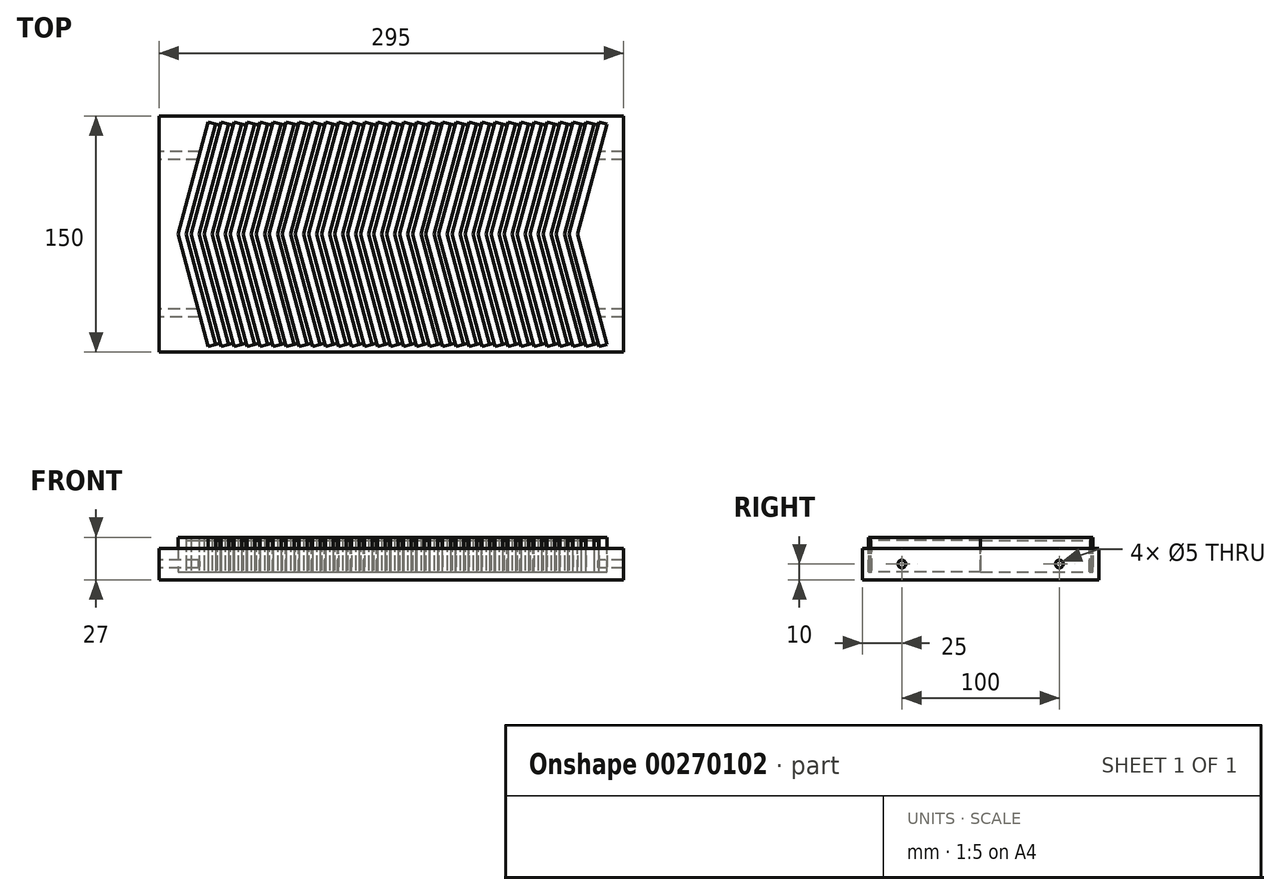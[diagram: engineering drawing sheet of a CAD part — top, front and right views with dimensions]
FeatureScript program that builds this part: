
annotation { "Feature Type Name" : "Feature", "Feature Type Description" : "" }
export const myFeature = defineFeature(function(context is Context, id is Id, definition is map)
    precondition{}
    {
        {
            var Q0;
            Q0=qCreatedBy(makeId("Top.planeOp"),FACE);
            var sketch = newSketch(context, id + "F0", { "sketchPlane" : qUnion([Q0])});
            skLineSegment(sketch, "E0.bottom", {"start": v(147.5, -75) * mm, "end": v(-147.5, -75) * mm});
            skLineSegment(sketch, "E0.top", {"start": v(147.5, 75) * mm, "end": v(-147.5, 75) * mm});
            skLineSegment(sketch, "E0.left", {"start": v(147.5, -75) * mm, "end": v(147.5, 75) * mm});
            skLineSegment(sketch, "E0.right", {"start": v(-147.5, -75) * mm, "end": v(-147.5, 75) * mm});
            skPoint(sketch, "E0.middle", {"position": v(0, 0) * mm});
            skPoint(sketch, "E1", {"position": v(0, 75) * mm});
            skPoint(sketch, "E2", {"position": v(-147.5, 0) * mm});
            skSolve(sketch);
        }
        {
            var Q0;
            Q0=makeQuery(id+"F0.imprint","IMPRINT",FACE,{"disambiguationData":[TD([[makeQuery(id+"F0.imprint","IMPRINT",EDGE,{"derivedFrom":sQuery(id+"F0.wireOp",EDGE,"E0.bottom")}),-1.0]])]});
            extrude(context, id + "F1", {"entities" : qUnion([Q0]), "depth" : 20 * mm});
        }
        {
            var Q0;
            Q0=makeQuery(id+"F1.opExtrude","SWEPT_FACE",FACE,{"disambiguationData":[OSD([sQuery(id+"F0.wireOp",EDGE,"E0.left")])]});
            var sketch = newSketch(context, id + "F2", { "sketchPlane" : qUnion([Q0])});
            skPoint(sketch, "E3", {"position": v(-50, 10) * mm});
            skPoint(sketch, "E4", {"position": v(50, 10) * mm});
            skSolve(sketch);
        }
        {
            var Q0;
            Q0=sQuery(id+"F2.wireOp",VERTEX,"E3");
            var Q1;
            Q1=sQuery(id+"F2.wireOp",VERTEX,"E4");
            var Q2;
            Q2=makeQuery(id+"F1.opExtrude","SWEPT_BODY",BODY,{"disambiguationData":[OSD([sQuery(id+"F0.wireOp",EDGE,"E0.bottom"),sQuery(id+"F0.wireOp",EDGE,"E0.top"),sQuery(id+"F0.wireOp",EDGE,"E0.left"),sQuery(id+"F0.wireOp",EDGE,"E0.right")])]});
            hole(context, id + "F3", {"style" : HoleStyle.SIMPLE, "endStyle" : HoleEndStyle.THROUGH, "standardTappedOrClearance" : lookupTablePath({ "standard" : "ISO", "engagement" : "75%", "pitch" : "1 mm", "size" : "M6", "type" : "Tapped" }), "standardBlindInLast" : lookupTablePath({ "standard" : "ISO", "engagement" : "75%", "pitch" : "1 mm", "size" : "M6", "type" : "Tapped" }), "holeDiameter" : 5 * mm, "showTappedDepth" : true, "tappedDepth" : 40 * mm, "tapClearance" : 3, "startFromSketch" : true, "locations" : qUnion([Q0, Q1]), "scope" : qUnion([Q2]), "majorDiameter" : 6 * mm});
        }
        {
            var Q0;
            Q0=makeQuery(id+"F1.opExtrude","SWEPT_FACE",FACE,{"disambiguationData":[OSD([sQuery(id+"F0.wireOp",EDGE,"E0.right")])]});
            var sketch = newSketch(context, id + "F4", { "sketchPlane" : qUnion([Q0])});
            skPoint(sketch, "E5", {"position": v(0, 10) * mm});
            skLineSegment(sketch, "E6", {"start": v(-50, 10) * mm, "end": v(50, 10) * mm, "construction": true});
            skSolve(sketch);
        }
        {
            var Q0;
            Q0=makeQuery(id+"F1.opExtrude","CAP_FACE",FACE,{"disambiguationData":[OSD([sQuery(id+"F0.wireOp",EDGE,"E0.bottom"),sQuery(id+"F0.wireOp",EDGE,"E0.top"),sQuery(id+"F0.wireOp",EDGE,"E0.left"),sQuery(id+"F0.wireOp",EDGE,"E0.right")])],"isStart":false});
            var sketch = newSketch(context, id + "F5", { "sketchPlane" : qUnion([Q0])});
            skLineSegment(sketch, "E7", {"start": v(-135.5, 0) * mm, "end": v(-116.4, 71.3) * mm});
            skLineSegment(sketch, "E8", {"start": v(-135.5, 0) * mm, "end": v(-116.4, -71.3) * mm});
            skLineSegment(sketch, "E9.0", {"start": v(-130.32, 0) * mm, "end": v(-111.57, 70) * mm});
            skLineSegment(sketch, "E9.1", {"start": v(-130.32, 0) * mm, "end": v(-111.57, -70) * mm});
            skLineSegment(sketch, "E10", {"start": v(-116.4, 71.3) * mm, "end": v(-111.57, 70) * mm});
            skLineSegment(sketch, "E11", {"start": v(-116.4, -71.3) * mm, "end": v(-111.57, -70) * mm});
            skLineSegment(sketch, "E12.0", {"start": v(-127.22, 0) * mm, "end": v(-108.67, 69.22) * mm});
            skLineSegment(sketch, "E12.1", {"start": v(-127.22, 0) * mm, "end": v(-108.67, -69.22) * mm});
            skLineSegment(sketch, "E13", {"start": v(-111.57, 70) * mm, "end": v(-108.67, 69.22) * mm});
            skLineSegment(sketch, "E14", {"start": v(-111.57, -70) * mm, "end": v(-108.67, -69.22) * mm});
            skLineSegment(sketch, "E15.1.0.0", {"start": v(-118.94, 0) * mm, "end": v(-100.39, 69.22) * mm});
            skLineSegment(sketch, "E15.1.0.1", {"start": v(-122.04, 0) * mm, "end": v(-103.28, 70) * mm});
            skLineSegment(sketch, "E15.1.0.2", {"start": v(-127.22, 0) * mm, "end": v(-108.11, 71.3) * mm});
            skLineSegment(sketch, "E15.1.0.3", {"start": v(-127.22, 0) * mm, "end": v(-108.11, -71.3) * mm});
            skLineSegment(sketch, "E15.1.0.4", {"start": v(-122.04, 0) * mm, "end": v(-103.28, -70) * mm});
            skLineSegment(sketch, "E15.1.0.5", {"start": v(-118.94, 0) * mm, "end": v(-100.39, -69.22) * mm});
            skLineSegment(sketch, "E15.1.0.6", {"start": v(-108.11, -71.3) * mm, "end": v(-103.28, -70) * mm});
            skLineSegment(sketch, "E15.1.0.7", {"start": v(-103.28, -70) * mm, "end": v(-100.39, -69.22) * mm});
            skLineSegment(sketch, "E15.1.0.8", {"start": v(-108.11, 71.3) * mm, "end": v(-103.28, 70) * mm});
            skLineSegment(sketch, "E15.1.0.9", {"start": v(-103.28, 70) * mm, "end": v(-100.39, 69.22) * mm});
            skLineSegment(sketch, "E15.2.0.0", {"start": v(-110.65, 0) * mm, "end": v(-92.1, 69.22) * mm});
            skLineSegment(sketch, "E15.2.0.1", {"start": v(-113.76, 0) * mm, "end": v(-95, 70) * mm});
            skLineSegment(sketch, "E15.2.0.2", {"start": v(-118.94, 0) * mm, "end": v(-99.83, 71.3) * mm});
            skLineSegment(sketch, "E15.2.0.3", {"start": v(-118.94, 0) * mm, "end": v(-99.83, -71.3) * mm});
            skLineSegment(sketch, "E15.2.0.4", {"start": v(-113.76, 0) * mm, "end": v(-95, -70) * mm});
            skLineSegment(sketch, "E15.2.0.5", {"start": v(-110.65, 0) * mm, "end": v(-92.1, -69.22) * mm});
            skLineSegment(sketch, "E15.2.0.6", {"start": v(-99.83, -71.3) * mm, "end": v(-95, -70) * mm});
            skLineSegment(sketch, "E15.2.0.7", {"start": v(-95, -70) * mm, "end": v(-92.1, -69.22) * mm});
            skLineSegment(sketch, "E15.2.0.8", {"start": v(-99.83, 71.3) * mm, "end": v(-95, 70) * mm});
            skLineSegment(sketch, "E15.2.0.9", {"start": v(-95, 70) * mm, "end": v(-92.1, 69.22) * mm});
            skLineSegment(sketch, "E15.direction1", {"start": v(-127.22, 0) * mm, "end": v(-118.94, 0) * mm, "construction": true});
            skLineSegment(sketch, "E16.0.3.0", {"start": v(-102.37, 0) * mm, "end": v(-83.82, 69.22) * mm});
            skLineSegment(sketch, "E16.3.3.0", {"start": v(-105.48, 0) * mm, "end": v(-86.72, 70) * mm});
            skLineSegment(sketch, "E16.6.3.0", {"start": v(-110.65, 0) * mm, "end": v(-91.55, 71.3) * mm});
            skLineSegment(sketch, "E16.9.3.0", {"start": v(-110.65, 0) * mm, "end": v(-91.55, -71.3) * mm});
            skLineSegment(sketch, "E16.12.3.0", {"start": v(-105.48, 0) * mm, "end": v(-86.72, -70) * mm});
            skLineSegment(sketch, "E16.15.3.0", {"start": v(-102.37, 0) * mm, "end": v(-83.82, -69.22) * mm});
            skLineSegment(sketch, "E16.18.3.0", {"start": v(-91.55, -71.3) * mm, "end": v(-86.72, -70) * mm});
            skLineSegment(sketch, "E16.21.3.0", {"start": v(-86.72, -70) * mm, "end": v(-83.82, -69.22) * mm});
            skLineSegment(sketch, "E16.24.3.0", {"start": v(-91.55, 71.3) * mm, "end": v(-86.72, 70) * mm});
            skLineSegment(sketch, "E16.27.3.0", {"start": v(-86.72, 70) * mm, "end": v(-83.82, 69.22) * mm});
            skLineSegment(sketch, "E16.0.4.0", {"start": v(-94.09, 0) * mm, "end": v(-75.54, 69.22) * mm});
            skLineSegment(sketch, "E16.3.4.0", {"start": v(-97.2, 0) * mm, "end": v(-78.44, 70) * mm});
            skLineSegment(sketch, "E16.6.4.0", {"start": v(-102.37, 0) * mm, "end": v(-83.27, 71.3) * mm});
            skLineSegment(sketch, "E16.9.4.0", {"start": v(-102.37, 0) * mm, "end": v(-83.27, -71.3) * mm});
            skLineSegment(sketch, "E16.12.4.0", {"start": v(-97.2, 0) * mm, "end": v(-78.44, -70) * mm});
            skLineSegment(sketch, "E16.15.4.0", {"start": v(-94.09, 0) * mm, "end": v(-75.54, -69.22) * mm});
            skLineSegment(sketch, "E16.18.4.0", {"start": v(-83.27, -71.3) * mm, "end": v(-78.44, -70) * mm});
            skLineSegment(sketch, "E16.21.4.0", {"start": v(-78.44, -70) * mm, "end": v(-75.54, -69.22) * mm});
            skLineSegment(sketch, "E16.24.4.0", {"start": v(-83.27, 71.3) * mm, "end": v(-78.44, 70) * mm});
            skLineSegment(sketch, "E16.27.4.0", {"start": v(-78.44, 70) * mm, "end": v(-75.54, 69.22) * mm});
            skLineSegment(sketch, "E16.0.5.0", {"start": v(-85.8, 0) * mm, "end": v(-67.26, 69.22) * mm});
            skLineSegment(sketch, "E16.3.5.0", {"start": v(-88.91, 0) * mm, "end": v(-70.16, 70) * mm});
            skLineSegment(sketch, "E16.6.5.0", {"start": v(-94.09, 0) * mm, "end": v(-74.99, 71.3) * mm});
            skLineSegment(sketch, "E16.9.5.0", {"start": v(-94.09, 0) * mm, "end": v(-74.99, -71.3) * mm});
            skLineSegment(sketch, "E16.12.5.0", {"start": v(-88.91, 0) * mm, "end": v(-70.16, -70) * mm});
            skLineSegment(sketch, "E16.15.5.0", {"start": v(-85.8, 0) * mm, "end": v(-67.26, -69.22) * mm});
            skLineSegment(sketch, "E16.18.5.0", {"start": v(-74.99, -71.3) * mm, "end": v(-70.16, -70) * mm});
            skLineSegment(sketch, "E16.21.5.0", {"start": v(-70.16, -70) * mm, "end": v(-67.26, -69.22) * mm});
            skLineSegment(sketch, "E16.24.5.0", {"start": v(-74.99, 71.3) * mm, "end": v(-70.16, 70) * mm});
            skLineSegment(sketch, "E16.27.5.0", {"start": v(-70.16, 70) * mm, "end": v(-67.26, 69.22) * mm});
            skLineSegment(sketch, "E16.0.6.0", {"start": v(-77.52, 0) * mm, "end": v(-58.98, 69.22) * mm});
            skLineSegment(sketch, "E16.3.6.0", {"start": v(-80.63, 0) * mm, "end": v(-61.87, 70) * mm});
            skLineSegment(sketch, "E16.6.6.0", {"start": v(-85.8, 0) * mm, "end": v(-66.7, 71.3) * mm});
            skLineSegment(sketch, "E16.9.6.0", {"start": v(-85.8, 0) * mm, "end": v(-66.7, -71.3) * mm});
            skLineSegment(sketch, "E16.12.6.0", {"start": v(-80.63, 0) * mm, "end": v(-61.87, -70) * mm});
            skLineSegment(sketch, "E16.15.6.0", {"start": v(-77.52, 0) * mm, "end": v(-58.98, -69.22) * mm});
            skLineSegment(sketch, "E16.18.6.0", {"start": v(-66.7, -71.3) * mm, "end": v(-61.87, -70) * mm});
            skLineSegment(sketch, "E16.21.6.0", {"start": v(-61.87, -70) * mm, "end": v(-58.98, -69.22) * mm});
            skLineSegment(sketch, "E16.24.6.0", {"start": v(-66.7, 71.3) * mm, "end": v(-61.87, 70) * mm});
            skLineSegment(sketch, "E16.27.6.0", {"start": v(-61.87, 70) * mm, "end": v(-58.98, 69.22) * mm});
            skLineSegment(sketch, "E16.0.7.0", {"start": v(-69.24, 0) * mm, "end": v(-50.7, 69.22) * mm});
            skLineSegment(sketch, "E16.3.7.0", {"start": v(-72.35, 0) * mm, "end": v(-53.6, 70) * mm});
            skLineSegment(sketch, "E16.6.7.0", {"start": v(-77.52, 0) * mm, "end": v(-58.42, 71.3) * mm});
            skLineSegment(sketch, "E16.9.7.0", {"start": v(-77.52, 0) * mm, "end": v(-58.42, -71.3) * mm});
            skLineSegment(sketch, "E16.12.7.0", {"start": v(-72.35, 0) * mm, "end": v(-53.6, -70) * mm});
            skLineSegment(sketch, "E16.15.7.0", {"start": v(-69.24, 0) * mm, "end": v(-50.7, -69.22) * mm});
            skLineSegment(sketch, "E16.18.7.0", {"start": v(-58.42, -71.3) * mm, "end": v(-53.6, -70) * mm});
            skLineSegment(sketch, "E16.21.7.0", {"start": v(-53.6, -70) * mm, "end": v(-50.7, -69.22) * mm});
            skLineSegment(sketch, "E16.24.7.0", {"start": v(-58.42, 71.3) * mm, "end": v(-53.6, 70) * mm});
            skLineSegment(sketch, "E16.27.7.0", {"start": v(-53.6, 70) * mm, "end": v(-50.7, 69.22) * mm});
            skLineSegment(sketch, "E16.0.8.0", {"start": v(-60.96, 0) * mm, "end": v(-42.41, 69.22) * mm});
            skLineSegment(sketch, "E16.3.8.0", {"start": v(-64.07, 0) * mm, "end": v(-45.3, 70) * mm});
            skLineSegment(sketch, "E16.6.8.0", {"start": v(-69.24, 0) * mm, "end": v(-50.14, 71.3) * mm});
            skLineSegment(sketch, "E16.9.8.0", {"start": v(-69.24, 0) * mm, "end": v(-50.14, -71.3) * mm});
            skLineSegment(sketch, "E16.12.8.0", {"start": v(-64.07, 0) * mm, "end": v(-45.3, -70) * mm});
            skLineSegment(sketch, "E16.15.8.0", {"start": v(-60.96, 0) * mm, "end": v(-42.41, -69.22) * mm});
            skLineSegment(sketch, "E16.18.8.0", {"start": v(-50.14, -71.3) * mm, "end": v(-45.3, -70) * mm});
            skLineSegment(sketch, "E16.21.8.0", {"start": v(-45.3, -70) * mm, "end": v(-42.41, -69.22) * mm});
            skLineSegment(sketch, "E16.24.8.0", {"start": v(-50.14, 71.3) * mm, "end": v(-45.3, 70) * mm});
            skLineSegment(sketch, "E16.27.8.0", {"start": v(-45.3, 70) * mm, "end": v(-42.41, 69.22) * mm});
            skLineSegment(sketch, "E16.0.9.0", {"start": v(-52.68, 0) * mm, "end": v(-34.13, 69.22) * mm});
            skLineSegment(sketch, "E16.3.9.0", {"start": v(-55.78, 0) * mm, "end": v(-37.03, 70) * mm});
            skLineSegment(sketch, "E16.6.9.0", {"start": v(-60.96, 0) * mm, "end": v(-41.86, 71.3) * mm});
            skLineSegment(sketch, "E16.9.9.0", {"start": v(-60.96, 0) * mm, "end": v(-41.86, -71.3) * mm});
            skLineSegment(sketch, "E16.12.9.0", {"start": v(-55.78, 0) * mm, "end": v(-37.03, -70) * mm});
            skLineSegment(sketch, "E16.15.9.0", {"start": v(-52.68, 0) * mm, "end": v(-34.13, -69.22) * mm});
            skLineSegment(sketch, "E16.18.9.0", {"start": v(-41.86, -71.3) * mm, "end": v(-37.03, -70) * mm});
            skLineSegment(sketch, "E16.21.9.0", {"start": v(-37.03, -70) * mm, "end": v(-34.13, -69.22) * mm});
            skLineSegment(sketch, "E16.24.9.0", {"start": v(-41.86, 71.3) * mm, "end": v(-37.03, 70) * mm});
            skLineSegment(sketch, "E16.27.9.0", {"start": v(-37.03, 70) * mm, "end": v(-34.13, 69.22) * mm});
            skLineSegment(sketch, "E16.0.10.0", {"start": v(-44.4, 0) * mm, "end": v(-25.85, 69.22) * mm});
            skLineSegment(sketch, "E16.3.10.0", {"start": v(-47.5, 0) * mm, "end": v(-28.75, 70) * mm});
            skLineSegment(sketch, "E16.6.10.0", {"start": v(-52.68, 0) * mm, "end": v(-33.57, 71.3) * mm});
            skLineSegment(sketch, "E16.9.10.0", {"start": v(-52.68, 0) * mm, "end": v(-33.57, -71.3) * mm});
            skLineSegment(sketch, "E16.12.10.0", {"start": v(-47.5, 0) * mm, "end": v(-28.75, -70) * mm});
            skLineSegment(sketch, "E16.15.10.0", {"start": v(-44.4, 0) * mm, "end": v(-25.85, -69.22) * mm});
            skLineSegment(sketch, "E16.18.10.0", {"start": v(-33.57, -71.3) * mm, "end": v(-28.75, -70) * mm});
            skLineSegment(sketch, "E16.21.10.0", {"start": v(-28.75, -70) * mm, "end": v(-25.85, -69.22) * mm});
            skLineSegment(sketch, "E16.24.10.0", {"start": v(-33.57, 71.3) * mm, "end": v(-28.75, 70) * mm});
            skLineSegment(sketch, "E16.27.10.0", {"start": v(-28.75, 70) * mm, "end": v(-25.85, 69.22) * mm});
            skLineSegment(sketch, "E16.0.11.0", {"start": v(-36.11, 0) * mm, "end": v(-17.57, 69.22) * mm});
            skLineSegment(sketch, "E16.3.11.0", {"start": v(-39.22, 0) * mm, "end": v(-20.46, 70) * mm});
            skLineSegment(sketch, "E16.6.11.0", {"start": v(-44.4, 0) * mm, "end": v(-25.3, 71.3) * mm});
            skLineSegment(sketch, "E16.9.11.0", {"start": v(-44.4, 0) * mm, "end": v(-25.3, -71.3) * mm});
            skLineSegment(sketch, "E16.12.11.0", {"start": v(-39.22, 0) * mm, "end": v(-20.46, -70) * mm});
            skLineSegment(sketch, "E16.15.11.0", {"start": v(-36.11, 0) * mm, "end": v(-17.57, -69.22) * mm});
            skLineSegment(sketch, "E16.18.11.0", {"start": v(-25.3, -71.3) * mm, "end": v(-20.46, -70) * mm});
            skLineSegment(sketch, "E16.21.11.0", {"start": v(-20.46, -70) * mm, "end": v(-17.57, -69.22) * mm});
            skLineSegment(sketch, "E16.24.11.0", {"start": v(-25.3, 71.3) * mm, "end": v(-20.46, 70) * mm});
            skLineSegment(sketch, "E16.27.11.0", {"start": v(-20.46, 70) * mm, "end": v(-17.57, 69.22) * mm});
            skLineSegment(sketch, "E16.0.12.0", {"start": v(-27.83, 0) * mm, "end": v(-9.28, 69.22) * mm});
            skLineSegment(sketch, "E16.3.12.0", {"start": v(-30.94, 0) * mm, "end": v(-12.18, 70) * mm});
            skLineSegment(sketch, "E16.6.12.0", {"start": v(-36.11, 0) * mm, "end": v(-17.01, 71.3) * mm});
            skLineSegment(sketch, "E16.9.12.0", {"start": v(-36.11, 0) * mm, "end": v(-17.01, -71.3) * mm});
            skLineSegment(sketch, "E16.12.12.0", {"start": v(-30.94, 0) * mm, "end": v(-12.18, -70) * mm});
            skLineSegment(sketch, "E16.15.12.0", {"start": v(-27.83, 0) * mm, "end": v(-9.28, -69.22) * mm});
            skLineSegment(sketch, "E16.18.12.0", {"start": v(-17.01, -71.3) * mm, "end": v(-12.18, -70) * mm});
            skLineSegment(sketch, "E16.21.12.0", {"start": v(-12.18, -70) * mm, "end": v(-9.28, -69.22) * mm});
            skLineSegment(sketch, "E16.24.12.0", {"start": v(-17.01, 71.3) * mm, "end": v(-12.18, 70) * mm});
            skLineSegment(sketch, "E16.27.12.0", {"start": v(-12.18, 70) * mm, "end": v(-9.28, 69.22) * mm});
            skLineSegment(sketch, "E16.0.13.0", {"start": v(-19.55, 0) * mm, "end": v(-1, 69.22) * mm});
            skLineSegment(sketch, "E16.3.13.0", {"start": v(-22.65, 0) * mm, "end": v(-3.9, 70) * mm});
            skLineSegment(sketch, "E16.6.13.0", {"start": v(-27.83, 0) * mm, "end": v(-8.73, 71.3) * mm});
            skLineSegment(sketch, "E16.9.13.0", {"start": v(-27.83, 0) * mm, "end": v(-8.73, -71.3) * mm});
            skLineSegment(sketch, "E16.12.13.0", {"start": v(-22.65, 0) * mm, "end": v(-3.9, -70) * mm});
            skLineSegment(sketch, "E16.15.13.0", {"start": v(-19.55, 0) * mm, "end": v(-1, -69.22) * mm});
            skLineSegment(sketch, "E16.18.13.0", {"start": v(-8.73, -71.3) * mm, "end": v(-3.9, -70) * mm});
            skLineSegment(sketch, "E16.21.13.0", {"start": v(-3.9, -70) * mm, "end": v(-1, -69.22) * mm});
            skLineSegment(sketch, "E16.24.13.0", {"start": v(-8.73, 71.3) * mm, "end": v(-3.9, 70) * mm});
            skLineSegment(sketch, "E16.27.13.0", {"start": v(-3.9, 70) * mm, "end": v(-1, 69.22) * mm});
            skLineSegment(sketch, "E16.0.14.0", {"start": v(-11.27, 0) * mm, "end": v(7.28, 69.22) * mm});
            skLineSegment(sketch, "E16.3.14.0", {"start": v(-14.37, 0) * mm, "end": v(4.38, 70) * mm});
            skLineSegment(sketch, "E16.6.14.0", {"start": v(-19.55, 0) * mm, "end": v(-0.45, 71.3) * mm});
            skLineSegment(sketch, "E16.9.14.0", {"start": v(-19.55, 0) * mm, "end": v(-0.45, -71.3) * mm});
            skLineSegment(sketch, "E16.12.14.0", {"start": v(-14.37, 0) * mm, "end": v(4.38, -70) * mm});
            skLineSegment(sketch, "E16.15.14.0", {"start": v(-11.27, 0) * mm, "end": v(7.28, -69.22) * mm});
            skLineSegment(sketch, "E16.18.14.0", {"start": v(-0.45, -71.3) * mm, "end": v(4.38, -70) * mm});
            skLineSegment(sketch, "E16.21.14.0", {"start": v(4.38, -70) * mm, "end": v(7.28, -69.22) * mm});
            skLineSegment(sketch, "E16.24.14.0", {"start": v(-0.45, 71.3) * mm, "end": v(4.38, 70) * mm});
            skLineSegment(sketch, "E16.27.14.0", {"start": v(4.38, 70) * mm, "end": v(7.28, 69.22) * mm});
            skLineSegment(sketch, "E16.0.15.0", {"start": v(-2.98, 0) * mm, "end": v(15.56, 69.22) * mm});
            skLineSegment(sketch, "E16.3.15.0", {"start": v(-6.1, 0) * mm, "end": v(12.67, 70) * mm});
            skLineSegment(sketch, "E16.6.15.0", {"start": v(-11.27, 0) * mm, "end": v(7.84, 71.3) * mm});
            skLineSegment(sketch, "E16.9.15.0", {"start": v(-11.27, 0) * mm, "end": v(7.84, -71.3) * mm});
            skLineSegment(sketch, "E16.12.15.0", {"start": v(-6.1, 0) * mm, "end": v(12.67, -70) * mm});
            skLineSegment(sketch, "E16.15.15.0", {"start": v(-2.98, 0) * mm, "end": v(15.56, -69.22) * mm});
            skLineSegment(sketch, "E16.18.15.0", {"start": v(7.84, -71.3) * mm, "end": v(12.67, -70) * mm});
            skLineSegment(sketch, "E16.21.15.0", {"start": v(12.67, -70) * mm, "end": v(15.56, -69.22) * mm});
            skLineSegment(sketch, "E16.24.15.0", {"start": v(7.84, 71.3) * mm, "end": v(12.67, 70) * mm});
            skLineSegment(sketch, "E16.27.15.0", {"start": v(12.67, 70) * mm, "end": v(15.56, 69.22) * mm});
            skLineSegment(sketch, "E16.0.16.0", {"start": v(5.3, 0) * mm, "end": v(23.85, 69.22) * mm});
            skLineSegment(sketch, "E16.3.16.0", {"start": v(2.2, 0) * mm, "end": v(20.95, 70) * mm});
            skLineSegment(sketch, "E16.6.16.0", {"start": v(-2.98, 0) * mm, "end": v(16.12, 71.3) * mm});
            skLineSegment(sketch, "E16.9.16.0", {"start": v(-2.98, 0) * mm, "end": v(16.12, -71.3) * mm});
            skLineSegment(sketch, "E16.12.16.0", {"start": v(2.2, 0) * mm, "end": v(20.95, -70) * mm});
            skLineSegment(sketch, "E16.15.16.0", {"start": v(5.3, 0) * mm, "end": v(23.85, -69.22) * mm});
            skLineSegment(sketch, "E16.18.16.0", {"start": v(16.12, -71.3) * mm, "end": v(20.95, -70) * mm});
            skLineSegment(sketch, "E16.21.16.0", {"start": v(20.95, -70) * mm, "end": v(23.85, -69.22) * mm});
            skLineSegment(sketch, "E16.24.16.0", {"start": v(16.12, 71.3) * mm, "end": v(20.95, 70) * mm});
            skLineSegment(sketch, "E16.27.16.0", {"start": v(20.95, 70) * mm, "end": v(23.85, 69.22) * mm});
            skLineSegment(sketch, "E16.0.17.0", {"start": v(13.58, 0) * mm, "end": v(32.13, 69.22) * mm});
            skLineSegment(sketch, "E16.3.17.0", {"start": v(10.47, 0) * mm, "end": v(29.23, 70) * mm});
            skLineSegment(sketch, "E16.6.17.0", {"start": v(5.3, 0) * mm, "end": v(24.4, 71.3) * mm});
            skLineSegment(sketch, "E16.9.17.0", {"start": v(5.3, 0) * mm, "end": v(24.4, -71.3) * mm});
            skLineSegment(sketch, "E16.12.17.0", {"start": v(10.47, 0) * mm, "end": v(29.23, -70) * mm});
            skLineSegment(sketch, "E16.15.17.0", {"start": v(13.58, 0) * mm, "end": v(32.13, -69.22) * mm});
            skLineSegment(sketch, "E16.18.17.0", {"start": v(24.4, -71.3) * mm, "end": v(29.23, -70) * mm});
            skLineSegment(sketch, "E16.21.17.0", {"start": v(29.23, -70) * mm, "end": v(32.13, -69.22) * mm});
            skLineSegment(sketch, "E16.24.17.0", {"start": v(24.4, 71.3) * mm, "end": v(29.23, 70) * mm});
            skLineSegment(sketch, "E16.27.17.0", {"start": v(29.23, 70) * mm, "end": v(32.13, 69.22) * mm});
            skLineSegment(sketch, "E16.0.18.0", {"start": v(21.86, 0) * mm, "end": v(40.41, 69.22) * mm});
            skLineSegment(sketch, "E16.3.18.0", {"start": v(18.76, 0) * mm, "end": v(37.51, 70) * mm});
            skLineSegment(sketch, "E16.6.18.0", {"start": v(13.58, 0) * mm, "end": v(32.68, 71.3) * mm});
            skLineSegment(sketch, "E16.9.18.0", {"start": v(13.58, 0) * mm, "end": v(32.68, -71.3) * mm});
            skLineSegment(sketch, "E16.12.18.0", {"start": v(18.76, 0) * mm, "end": v(37.51, -70) * mm});
            skLineSegment(sketch, "E16.15.18.0", {"start": v(21.86, 0) * mm, "end": v(40.41, -69.22) * mm});
            skLineSegment(sketch, "E16.18.18.0", {"start": v(32.68, -71.3) * mm, "end": v(37.51, -70) * mm});
            skLineSegment(sketch, "E16.21.18.0", {"start": v(37.51, -70) * mm, "end": v(40.41, -69.22) * mm});
            skLineSegment(sketch, "E16.24.18.0", {"start": v(32.68, 71.3) * mm, "end": v(37.51, 70) * mm});
            skLineSegment(sketch, "E16.27.18.0", {"start": v(37.51, 70) * mm, "end": v(40.41, 69.22) * mm});
            skLineSegment(sketch, "E16.0.19.0", {"start": v(30.14, 0) * mm, "end": v(48.7, 69.22) * mm});
            skLineSegment(sketch, "E16.3.19.0", {"start": v(27.04, 0) * mm, "end": v(45.8, 70) * mm});
            skLineSegment(sketch, "E16.6.19.0", {"start": v(21.86, 0) * mm, "end": v(40.97, 71.3) * mm});
            skLineSegment(sketch, "E16.9.19.0", {"start": v(21.86, 0) * mm, "end": v(40.97, -71.3) * mm});
            skLineSegment(sketch, "E16.12.19.0", {"start": v(27.04, 0) * mm, "end": v(45.8, -70) * mm});
            skLineSegment(sketch, "E16.15.19.0", {"start": v(30.14, 0) * mm, "end": v(48.7, -69.22) * mm});
            skLineSegment(sketch, "E16.18.19.0", {"start": v(40.97, -71.3) * mm, "end": v(45.8, -70) * mm});
            skLineSegment(sketch, "E16.21.19.0", {"start": v(45.8, -70) * mm, "end": v(48.7, -69.22) * mm});
            skLineSegment(sketch, "E16.24.19.0", {"start": v(40.97, 71.3) * mm, "end": v(45.8, 70) * mm});
            skLineSegment(sketch, "E16.27.19.0", {"start": v(45.8, 70) * mm, "end": v(48.7, 69.22) * mm});
            skLineSegment(sketch, "E16.0.20.0", {"start": v(38.43, 0) * mm, "end": v(56.97, 69.22) * mm});
            skLineSegment(sketch, "E16.3.20.0", {"start": v(35.32, 0) * mm, "end": v(54.08, 70) * mm});
            skLineSegment(sketch, "E16.6.20.0", {"start": v(30.14, 0) * mm, "end": v(49.25, 71.3) * mm});
            skLineSegment(sketch, "E16.9.20.0", {"start": v(30.14, 0) * mm, "end": v(49.25, -71.3) * mm});
            skLineSegment(sketch, "E16.12.20.0", {"start": v(35.32, 0) * mm, "end": v(54.08, -70) * mm});
            skLineSegment(sketch, "E16.15.20.0", {"start": v(38.43, 0) * mm, "end": v(56.97, -69.22) * mm});
            skLineSegment(sketch, "E16.18.20.0", {"start": v(49.25, -71.3) * mm, "end": v(54.08, -70) * mm});
            skLineSegment(sketch, "E16.21.20.0", {"start": v(54.08, -70) * mm, "end": v(56.97, -69.22) * mm});
            skLineSegment(sketch, "E16.24.20.0", {"start": v(49.25, 71.3) * mm, "end": v(54.08, 70) * mm});
            skLineSegment(sketch, "E16.27.20.0", {"start": v(54.08, 70) * mm, "end": v(56.97, 69.22) * mm});
            skLineSegment(sketch, "E16.0.21.0", {"start": v(46.7, 0) * mm, "end": v(65.26, 69.22) * mm});
            skLineSegment(sketch, "E16.3.21.0", {"start": v(43.6, 0) * mm, "end": v(62.36, 70) * mm});
            skLineSegment(sketch, "E16.6.21.0", {"start": v(38.43, 0) * mm, "end": v(57.53, 71.3) * mm});
            skLineSegment(sketch, "E16.9.21.0", {"start": v(38.43, 0) * mm, "end": v(57.53, -71.3) * mm});
            skLineSegment(sketch, "E16.12.21.0", {"start": v(43.6, 0) * mm, "end": v(62.36, -70) * mm});
            skLineSegment(sketch, "E16.15.21.0", {"start": v(46.7, 0) * mm, "end": v(65.26, -69.22) * mm});
            skLineSegment(sketch, "E16.18.21.0", {"start": v(57.53, -71.3) * mm, "end": v(62.36, -70) * mm});
            skLineSegment(sketch, "E16.21.21.0", {"start": v(62.36, -70) * mm, "end": v(65.26, -69.22) * mm});
            skLineSegment(sketch, "E16.24.21.0", {"start": v(57.53, 71.3) * mm, "end": v(62.36, 70) * mm});
            skLineSegment(sketch, "E16.27.21.0", {"start": v(62.36, 70) * mm, "end": v(65.26, 69.22) * mm});
            skLineSegment(sketch, "E16.0.22.0", {"start": v(55, 0) * mm, "end": v(73.54, 69.22) * mm});
            skLineSegment(sketch, "E16.3.22.0", {"start": v(51.89, 0) * mm, "end": v(70.64, 70) * mm});
            skLineSegment(sketch, "E16.6.22.0", {"start": v(46.7, 0) * mm, "end": v(65.81, 71.3) * mm});
            skLineSegment(sketch, "E16.9.22.0", {"start": v(46.7, 0) * mm, "end": v(65.81, -71.3) * mm});
            skLineSegment(sketch, "E16.12.22.0", {"start": v(51.89, 0) * mm, "end": v(70.64, -70) * mm});
            skLineSegment(sketch, "E16.15.22.0", {"start": v(55, 0) * mm, "end": v(73.54, -69.22) * mm});
            skLineSegment(sketch, "E16.18.22.0", {"start": v(65.81, -71.3) * mm, "end": v(70.64, -70) * mm});
            skLineSegment(sketch, "E16.21.22.0", {"start": v(70.64, -70) * mm, "end": v(73.54, -69.22) * mm});
            skLineSegment(sketch, "E16.24.22.0", {"start": v(65.81, 71.3) * mm, "end": v(70.64, 70) * mm});
            skLineSegment(sketch, "E16.27.22.0", {"start": v(70.64, 70) * mm, "end": v(73.54, 69.22) * mm});
            skLineSegment(sketch, "E17.0.23.0", {"start": v(63.27, 0) * mm, "end": v(81.82, 69.22) * mm});
            skLineSegment(sketch, "E17.3.23.0", {"start": v(60.17, 0) * mm, "end": v(78.92, 70) * mm});
            skLineSegment(sketch, "E17.6.23.0", {"start": v(55, 0) * mm, "end": v(74.1, 71.3) * mm});
            skLineSegment(sketch, "E17.9.23.0", {"start": v(55, 0) * mm, "end": v(74.1, -71.3) * mm});
            skLineSegment(sketch, "E17.12.23.0", {"start": v(60.17, 0) * mm, "end": v(78.92, -70) * mm});
            skLineSegment(sketch, "E17.15.23.0", {"start": v(63.27, 0) * mm, "end": v(81.82, -69.22) * mm});
            skLineSegment(sketch, "E17.18.23.0", {"start": v(74.1, -71.3) * mm, "end": v(78.92, -70) * mm});
            skLineSegment(sketch, "E17.21.23.0", {"start": v(78.92, -70) * mm, "end": v(81.82, -69.22) * mm});
            skLineSegment(sketch, "E17.24.23.0", {"start": v(74.1, 71.3) * mm, "end": v(78.92, 70) * mm});
            skLineSegment(sketch, "E17.27.23.0", {"start": v(78.92, 70) * mm, "end": v(81.82, 69.22) * mm});
            skLineSegment(sketch, "E17.0.24.0", {"start": v(71.56, 0) * mm, "end": v(90.1, 69.22) * mm});
            skLineSegment(sketch, "E17.3.24.0", {"start": v(68.45, 0) * mm, "end": v(87.2, 70) * mm});
            skLineSegment(sketch, "E17.6.24.0", {"start": v(63.27, 0) * mm, "end": v(82.38, 71.3) * mm});
            skLineSegment(sketch, "E17.9.24.0", {"start": v(63.27, 0) * mm, "end": v(82.38, -71.3) * mm});
            skLineSegment(sketch, "E17.12.24.0", {"start": v(68.45, 0) * mm, "end": v(87.2, -70) * mm});
            skLineSegment(sketch, "E17.15.24.0", {"start": v(71.56, 0) * mm, "end": v(90.1, -69.22) * mm});
            skLineSegment(sketch, "E17.18.24.0", {"start": v(82.38, -71.3) * mm, "end": v(87.2, -70) * mm});
            skLineSegment(sketch, "E17.21.24.0", {"start": v(87.2, -70) * mm, "end": v(90.1, -69.22) * mm});
            skLineSegment(sketch, "E17.24.24.0", {"start": v(82.38, 71.3) * mm, "end": v(87.2, 70) * mm});
            skLineSegment(sketch, "E17.27.24.0", {"start": v(87.2, 70) * mm, "end": v(90.1, 69.22) * mm});
            skLineSegment(sketch, "E18.0.25.0", {"start": v(79.84, 0) * mm, "end": v(98.39, 69.22) * mm});
            skLineSegment(sketch, "E18.3.25.0", {"start": v(76.73, 0) * mm, "end": v(95.49, 70) * mm});
            skLineSegment(sketch, "E18.6.25.0", {"start": v(71.56, 0) * mm, "end": v(90.66, 71.3) * mm});
            skLineSegment(sketch, "E18.9.25.0", {"start": v(71.56, 0) * mm, "end": v(90.66, -71.3) * mm});
            skLineSegment(sketch, "E18.12.25.0", {"start": v(76.73, 0) * mm, "end": v(95.49, -70) * mm});
            skLineSegment(sketch, "E18.15.25.0", {"start": v(79.84, 0) * mm, "end": v(98.39, -69.22) * mm});
            skLineSegment(sketch, "E18.18.25.0", {"start": v(90.66, -71.3) * mm, "end": v(95.49, -70) * mm});
            skLineSegment(sketch, "E18.21.25.0", {"start": v(95.49, -70) * mm, "end": v(98.39, -69.22) * mm});
            skLineSegment(sketch, "E18.24.25.0", {"start": v(90.66, 71.3) * mm, "end": v(95.49, 70) * mm});
            skLineSegment(sketch, "E18.27.25.0", {"start": v(95.49, 70) * mm, "end": v(98.39, 69.22) * mm});
            skLineSegment(sketch, "E18.0.26.0", {"start": v(88.12, 0) * mm, "end": v(106.67, 69.22) * mm});
            skLineSegment(sketch, "E18.3.26.0", {"start": v(85.01, 0) * mm, "end": v(103.77, 70) * mm});
            skLineSegment(sketch, "E18.6.26.0", {"start": v(79.84, 0) * mm, "end": v(98.94, 71.3) * mm});
            skLineSegment(sketch, "E18.9.26.0", {"start": v(79.84, 0) * mm, "end": v(98.94, -71.3) * mm});
            skLineSegment(sketch, "E18.12.26.0", {"start": v(85.01, 0) * mm, "end": v(103.77, -70) * mm});
            skLineSegment(sketch, "E18.15.26.0", {"start": v(88.12, 0) * mm, "end": v(106.67, -69.22) * mm});
            skLineSegment(sketch, "E18.18.26.0", {"start": v(98.94, -71.3) * mm, "end": v(103.77, -70) * mm});
            skLineSegment(sketch, "E18.21.26.0", {"start": v(103.77, -70) * mm, "end": v(106.67, -69.22) * mm});
            skLineSegment(sketch, "E18.24.26.0", {"start": v(98.94, 71.3) * mm, "end": v(103.77, 70) * mm});
            skLineSegment(sketch, "E18.27.26.0", {"start": v(103.77, 70) * mm, "end": v(106.67, 69.22) * mm});
            skLineSegment(sketch, "E18.0.27.0", {"start": v(96.4, 0) * mm, "end": v(114.95, 69.22) * mm});
            skLineSegment(sketch, "E18.3.27.0", {"start": v(93.3, 0) * mm, "end": v(112.05, 70) * mm});
            skLineSegment(sketch, "E18.6.27.0", {"start": v(88.12, 0) * mm, "end": v(107.22, 71.3) * mm});
            skLineSegment(sketch, "E18.9.27.0", {"start": v(88.12, 0) * mm, "end": v(107.22, -71.3) * mm});
            skLineSegment(sketch, "E18.12.27.0", {"start": v(93.3, 0) * mm, "end": v(112.05, -70) * mm});
            skLineSegment(sketch, "E18.15.27.0", {"start": v(96.4, 0) * mm, "end": v(114.95, -69.22) * mm});
            skLineSegment(sketch, "E18.18.27.0", {"start": v(107.22, -71.3) * mm, "end": v(112.05, -70) * mm});
            skLineSegment(sketch, "E18.21.27.0", {"start": v(112.05, -70) * mm, "end": v(114.95, -69.22) * mm});
            skLineSegment(sketch, "E18.24.27.0", {"start": v(107.22, 71.3) * mm, "end": v(112.05, 70) * mm});
            skLineSegment(sketch, "E18.27.27.0", {"start": v(112.05, 70) * mm, "end": v(114.95, 69.22) * mm});
            skLineSegment(sketch, "E19.0.28.0", {"start": v(104.68, 0) * mm, "end": v(123.23, 69.22) * mm});
            skLineSegment(sketch, "E19.3.28.0", {"start": v(101.58, 0) * mm, "end": v(120.33, 70) * mm});
            skLineSegment(sketch, "E19.6.28.0", {"start": v(96.4, 0) * mm, "end": v(115.5, 71.3) * mm});
            skLineSegment(sketch, "E19.9.28.0", {"start": v(96.4, 0) * mm, "end": v(115.5, -71.3) * mm});
            skLineSegment(sketch, "E19.12.28.0", {"start": v(101.58, 0) * mm, "end": v(120.33, -70) * mm});
            skLineSegment(sketch, "E19.15.28.0", {"start": v(104.68, 0) * mm, "end": v(123.23, -69.22) * mm});
            skLineSegment(sketch, "E19.18.28.0", {"start": v(115.5, -71.3) * mm, "end": v(120.33, -70) * mm});
            skLineSegment(sketch, "E19.21.28.0", {"start": v(120.33, -70) * mm, "end": v(123.23, -69.22) * mm});
            skLineSegment(sketch, "E19.24.28.0", {"start": v(115.5, 71.3) * mm, "end": v(120.33, 70) * mm});
            skLineSegment(sketch, "E19.27.28.0", {"start": v(120.33, 70) * mm, "end": v(123.23, 69.22) * mm});
            skLineSegment(sketch, "E19.0.29.0", {"start": v(112.97, 0) * mm, "end": v(131.51, 69.22) * mm});
            skLineSegment(sketch, "E19.3.29.0", {"start": v(109.86, 0) * mm, "end": v(128.62, 70) * mm});
            skLineSegment(sketch, "E19.6.29.0", {"start": v(104.68, 0) * mm, "end": v(123.79, 71.3) * mm});
            skLineSegment(sketch, "E19.9.29.0", {"start": v(104.68, 0) * mm, "end": v(123.79, -71.3) * mm});
            skLineSegment(sketch, "E19.12.29.0", {"start": v(109.86, 0) * mm, "end": v(128.62, -70) * mm});
            skLineSegment(sketch, "E19.15.29.0", {"start": v(112.97, 0) * mm, "end": v(131.51, -69.22) * mm});
            skLineSegment(sketch, "E19.18.29.0", {"start": v(123.79, -71.3) * mm, "end": v(128.62, -70) * mm});
            skLineSegment(sketch, "E19.21.29.0", {"start": v(128.62, -70) * mm, "end": v(131.51, -69.22) * mm});
            skLineSegment(sketch, "E19.24.29.0", {"start": v(123.79, 71.3) * mm, "end": v(128.62, 70) * mm});
            skLineSegment(sketch, "E19.27.29.0", {"start": v(128.62, 70) * mm, "end": v(131.51, 69.22) * mm});
            skLineSegment(sketch, "E20", {"start": v(112.97, 0) * mm, "end": v(132.07, 71.3) * mm});
            skLineSegment(sketch, "E21", {"start": v(112.97, 0) * mm, "end": v(132.07, -71.3) * mm});
            skLineSegment(sketch, "E22.0", {"start": v(118.14, 0) * mm, "end": v(136.9, 70) * mm});
            skLineSegment(sketch, "E22.1", {"start": v(118.14, 0) * mm, "end": v(136.9, -70) * mm});
            skLineSegment(sketch, "E23", {"start": v(132.07, 71.3) * mm, "end": v(136.9, 70) * mm});
            skLineSegment(sketch, "E24", {"start": v(132.07, -71.3) * mm, "end": v(136.9, -70) * mm});
            skSolve(sketch);
        }
        {
            var Q0;
            Q0=makeQuery(id+"F5.imprint","IMPRINT",FACE,{"disambiguationData":[TD([[makeQuery(id+"F5.imprint","IMPRINT",EDGE,{"derivedFrom":sQuery(id+"F5.wireOp",EDGE,"E7")}),-1.0]])]});
            var Q1;
            Q1=makeQuery(id+"F5.imprint","IMPRINT",FACE,{"disambiguationData":[TD([[makeQuery(id+"F5.imprint","IMPRINT",EDGE,{"derivedFrom":sQuery(id+"F5.wireOp",EDGE,"E9.0")}),-1.0]])]});
            var Q2;
            Q2=makeQuery(id+"F5.imprint","IMPRINT",FACE,{"disambiguationData":[TD([[makeQuery(id+"F5.imprint","IMPRINT",EDGE,{"derivedFrom":sQuery(id+"F5.wireOp",EDGE,"E15.1.0.1")}),1.0]])]});
            var Q3;
            Q3=makeQuery(id+"F5.imprint","IMPRINT",FACE,{"disambiguationData":[TD([[makeQuery(id+"F5.imprint","IMPRINT",EDGE,{"derivedFrom":sQuery(id+"F5.wireOp",EDGE,"E15.1.0.1")}),-1.0]])]});
            var Q4;
            Q4=makeQuery(id+"F5.imprint","IMPRINT",FACE,{"disambiguationData":[TD([[makeQuery(id+"F5.imprint","IMPRINT",EDGE,{"derivedFrom":sQuery(id+"F5.wireOp",EDGE,"E15.2.0.1")}),1.0]])]});
            var Q5;
            Q5=makeQuery(id+"F5.imprint","IMPRINT",FACE,{"disambiguationData":[TD([[makeQuery(id+"F5.imprint","IMPRINT",EDGE,{"derivedFrom":sQuery(id+"F5.wireOp",EDGE,"E15.2.0.1")}),-1.0]])]});
            var Q6;
            Q6=makeQuery(id+"F5.imprint","IMPRINT",FACE,{"disambiguationData":[TD([[makeQuery(id+"F5.imprint","IMPRINT",EDGE,{"derivedFrom":sQuery(id+"F5.wireOp",EDGE,"E16.3.3.0")}),1.0]])]});
            var Q7;
            Q7=makeQuery(id+"F5.imprint","IMPRINT",FACE,{"disambiguationData":[TD([[makeQuery(id+"F5.imprint","IMPRINT",EDGE,{"derivedFrom":sQuery(id+"F5.wireOp",EDGE,"E16.3.3.0")}),-1.0]])]});
            var Q8;
            Q8=makeQuery(id+"F5.imprint","IMPRINT",FACE,{"disambiguationData":[TD([[makeQuery(id+"F5.imprint","IMPRINT",EDGE,{"derivedFrom":sQuery(id+"F5.wireOp",EDGE,"E16.3.4.0")}),1.0]])]});
            var Q9;
            Q9=makeQuery(id+"F5.imprint","IMPRINT",FACE,{"disambiguationData":[TD([[makeQuery(id+"F5.imprint","IMPRINT",EDGE,{"derivedFrom":sQuery(id+"F5.wireOp",EDGE,"E16.3.4.0")}),-1.0]])]});
            var Q10;
            Q10=makeQuery(id+"F5.imprint","IMPRINT",FACE,{"disambiguationData":[TD([[makeQuery(id+"F5.imprint","IMPRINT",EDGE,{"derivedFrom":sQuery(id+"F5.wireOp",EDGE,"E16.3.5.0")}),1.0]])]});
            var Q11;
            Q11=makeQuery(id+"F5.imprint","IMPRINT",FACE,{"disambiguationData":[TD([[makeQuery(id+"F5.imprint","IMPRINT",EDGE,{"derivedFrom":sQuery(id+"F5.wireOp",EDGE,"E16.3.5.0")}),-1.0]])]});
            var Q12;
            Q12=makeQuery(id+"F5.imprint","IMPRINT",FACE,{"disambiguationData":[TD([[makeQuery(id+"F5.imprint","IMPRINT",EDGE,{"derivedFrom":sQuery(id+"F5.wireOp",EDGE,"E16.3.6.0")}),1.0]])]});
            var Q13;
            Q13=makeQuery(id+"F5.imprint","IMPRINT",FACE,{"disambiguationData":[TD([[makeQuery(id+"F5.imprint","IMPRINT",EDGE,{"derivedFrom":sQuery(id+"F5.wireOp",EDGE,"E16.3.6.0")}),-1.0]])]});
            var Q14;
            Q14=makeQuery(id+"F5.imprint","IMPRINT",FACE,{"disambiguationData":[TD([[makeQuery(id+"F5.imprint","IMPRINT",EDGE,{"derivedFrom":sQuery(id+"F5.wireOp",EDGE,"E16.3.7.0")}),1.0]])]});
            var Q15;
            Q15=makeQuery(id+"F5.imprint","IMPRINT",FACE,{"disambiguationData":[TD([[makeQuery(id+"F5.imprint","IMPRINT",EDGE,{"derivedFrom":sQuery(id+"F5.wireOp",EDGE,"E16.3.7.0")}),-1.0]])]});
            var Q16;
            Q16=makeQuery(id+"F5.imprint","IMPRINT",FACE,{"disambiguationData":[TD([[makeQuery(id+"F5.imprint","IMPRINT",EDGE,{"derivedFrom":sQuery(id+"F5.wireOp",EDGE,"E16.3.8.0")}),1.0]])]});
            var Q17;
            Q17=makeQuery(id+"F5.imprint","IMPRINT",FACE,{"disambiguationData":[TD([[makeQuery(id+"F5.imprint","IMPRINT",EDGE,{"derivedFrom":sQuery(id+"F5.wireOp",EDGE,"E16.3.8.0")}),-1.0]])]});
            var Q18;
            Q18=makeQuery(id+"F5.imprint","IMPRINT",FACE,{"disambiguationData":[TD([[makeQuery(id+"F5.imprint","IMPRINT",EDGE,{"derivedFrom":sQuery(id+"F5.wireOp",EDGE,"E16.3.9.0")}),1.0]])]});
            var Q19;
            Q19=makeQuery(id+"F5.imprint","IMPRINT",FACE,{"disambiguationData":[TD([[makeQuery(id+"F5.imprint","IMPRINT",EDGE,{"derivedFrom":sQuery(id+"F5.wireOp",EDGE,"E16.3.9.0")}),-1.0]])]});
            var Q20;
            Q20=makeQuery(id+"F5.imprint","IMPRINT",FACE,{"disambiguationData":[TD([[makeQuery(id+"F5.imprint","IMPRINT",EDGE,{"derivedFrom":sQuery(id+"F5.wireOp",EDGE,"E16.3.10.0")}),1.0]])]});
            var Q21;
            Q21=makeQuery(id+"F5.imprint","IMPRINT",FACE,{"disambiguationData":[TD([[makeQuery(id+"F5.imprint","IMPRINT",EDGE,{"derivedFrom":sQuery(id+"F5.wireOp",EDGE,"E16.3.10.0")}),-1.0]])]});
            var Q22;
            Q22=makeQuery(id+"F5.imprint","IMPRINT",FACE,{"disambiguationData":[TD([[makeQuery(id+"F5.imprint","IMPRINT",EDGE,{"derivedFrom":sQuery(id+"F5.wireOp",EDGE,"E16.3.11.0")}),1.0]])]});
            var Q23;
            Q23=makeQuery(id+"F5.imprint","IMPRINT",FACE,{"disambiguationData":[TD([[makeQuery(id+"F5.imprint","IMPRINT",EDGE,{"derivedFrom":sQuery(id+"F5.wireOp",EDGE,"E16.3.11.0")}),-1.0]])]});
            var Q24;
            Q24=makeQuery(id+"F5.imprint","IMPRINT",FACE,{"disambiguationData":[TD([[makeQuery(id+"F5.imprint","IMPRINT",EDGE,{"derivedFrom":sQuery(id+"F5.wireOp",EDGE,"E16.3.12.0")}),1.0]])]});
            var Q25;
            Q25=makeQuery(id+"F5.imprint","IMPRINT",FACE,{"disambiguationData":[TD([[makeQuery(id+"F5.imprint","IMPRINT",EDGE,{"derivedFrom":sQuery(id+"F5.wireOp",EDGE,"E16.3.12.0")}),-1.0]])]});
            var Q26;
            Q26=makeQuery(id+"F5.imprint","IMPRINT",FACE,{"disambiguationData":[TD([[makeQuery(id+"F5.imprint","IMPRINT",EDGE,{"derivedFrom":sQuery(id+"F5.wireOp",EDGE,"E16.3.13.0")}),1.0]])]});
            var Q27;
            Q27=makeQuery(id+"F5.imprint","IMPRINT",FACE,{"disambiguationData":[TD([[makeQuery(id+"F5.imprint","IMPRINT",EDGE,{"derivedFrom":sQuery(id+"F5.wireOp",EDGE,"E16.3.13.0")}),-1.0]])]});
            var Q28;
            Q28=makeQuery(id+"F5.imprint","IMPRINT",FACE,{"disambiguationData":[TD([[makeQuery(id+"F5.imprint","IMPRINT",EDGE,{"derivedFrom":sQuery(id+"F5.wireOp",EDGE,"E16.3.14.0")}),1.0]])]});
            var Q29;
            Q29=makeQuery(id+"F5.imprint","IMPRINT",FACE,{"disambiguationData":[TD([[makeQuery(id+"F5.imprint","IMPRINT",EDGE,{"derivedFrom":sQuery(id+"F5.wireOp",EDGE,"E16.3.14.0")}),-1.0]])]});
            var Q30;
            Q30=makeQuery(id+"F5.imprint","IMPRINT",FACE,{"disambiguationData":[TD([[makeQuery(id+"F5.imprint","IMPRINT",EDGE,{"derivedFrom":sQuery(id+"F5.wireOp",EDGE,"E16.3.15.0")}),1.0]])]});
            var Q31;
            Q31=makeQuery(id+"F5.imprint","IMPRINT",FACE,{"disambiguationData":[TD([[makeQuery(id+"F5.imprint","IMPRINT",EDGE,{"derivedFrom":sQuery(id+"F5.wireOp",EDGE,"E16.3.15.0")}),-1.0]])]});
            var Q32;
            Q32=makeQuery(id+"F5.imprint","IMPRINT",FACE,{"disambiguationData":[TD([[makeQuery(id+"F5.imprint","IMPRINT",EDGE,{"derivedFrom":sQuery(id+"F5.wireOp",EDGE,"E16.3.16.0")}),1.0]])]});
            var Q33;
            Q33=makeQuery(id+"F5.imprint","IMPRINT",FACE,{"disambiguationData":[TD([[makeQuery(id+"F5.imprint","IMPRINT",EDGE,{"derivedFrom":sQuery(id+"F5.wireOp",EDGE,"E16.3.16.0")}),-1.0]])]});
            var Q34;
            Q34=makeQuery(id+"F5.imprint","IMPRINT",FACE,{"disambiguationData":[TD([[makeQuery(id+"F5.imprint","IMPRINT",EDGE,{"derivedFrom":sQuery(id+"F5.wireOp",EDGE,"E16.3.17.0")}),1.0]])]});
            var Q35;
            Q35=makeQuery(id+"F5.imprint","IMPRINT",FACE,{"disambiguationData":[TD([[makeQuery(id+"F5.imprint","IMPRINT",EDGE,{"derivedFrom":sQuery(id+"F5.wireOp",EDGE,"E16.3.17.0")}),-1.0]])]});
            var Q36;
            Q36=makeQuery(id+"F5.imprint","IMPRINT",FACE,{"disambiguationData":[TD([[makeQuery(id+"F5.imprint","IMPRINT",EDGE,{"derivedFrom":sQuery(id+"F5.wireOp",EDGE,"E16.3.18.0")}),1.0]])]});
            var Q37;
            Q37=makeQuery(id+"F5.imprint","IMPRINT",FACE,{"disambiguationData":[TD([[makeQuery(id+"F5.imprint","IMPRINT",EDGE,{"derivedFrom":sQuery(id+"F5.wireOp",EDGE,"E16.3.18.0")}),-1.0]])]});
            var Q38;
            Q38=makeQuery(id+"F5.imprint","IMPRINT",FACE,{"disambiguationData":[TD([[makeQuery(id+"F5.imprint","IMPRINT",EDGE,{"derivedFrom":sQuery(id+"F5.wireOp",EDGE,"E16.3.19.0")}),1.0]])]});
            var Q39;
            Q39=makeQuery(id+"F5.imprint","IMPRINT",FACE,{"disambiguationData":[TD([[makeQuery(id+"F5.imprint","IMPRINT",EDGE,{"derivedFrom":sQuery(id+"F5.wireOp",EDGE,"E16.3.19.0")}),-1.0]])]});
            var Q40;
            Q40=makeQuery(id+"F5.imprint","IMPRINT",FACE,{"disambiguationData":[TD([[makeQuery(id+"F5.imprint","IMPRINT",EDGE,{"derivedFrom":sQuery(id+"F5.wireOp",EDGE,"E16.3.20.0")}),1.0]])]});
            var Q41;
            Q41=makeQuery(id+"F5.imprint","IMPRINT",FACE,{"disambiguationData":[TD([[makeQuery(id+"F5.imprint","IMPRINT",EDGE,{"derivedFrom":sQuery(id+"F5.wireOp",EDGE,"E16.3.20.0")}),-1.0]])]});
            var Q42;
            Q42=makeQuery(id+"F5.imprint","IMPRINT",FACE,{"disambiguationData":[TD([[makeQuery(id+"F5.imprint","IMPRINT",EDGE,{"derivedFrom":sQuery(id+"F5.wireOp",EDGE,"E16.3.21.0")}),1.0]])]});
            var Q43;
            Q43=makeQuery(id+"F5.imprint","IMPRINT",FACE,{"disambiguationData":[TD([[makeQuery(id+"F5.imprint","IMPRINT",EDGE,{"derivedFrom":sQuery(id+"F5.wireOp",EDGE,"E16.3.21.0")}),-1.0]])]});
            var Q44;
            Q44=makeQuery(id+"F5.imprint","IMPRINT",FACE,{"disambiguationData":[TD([[makeQuery(id+"F5.imprint","IMPRINT",EDGE,{"derivedFrom":sQuery(id+"F5.wireOp",EDGE,"E16.3.22.0")}),1.0]])]});
            var Q45;
            Q45=makeQuery(id+"F5.imprint","IMPRINT",FACE,{"disambiguationData":[TD([[makeQuery(id+"F5.imprint","IMPRINT",EDGE,{"derivedFrom":sQuery(id+"F5.wireOp",EDGE,"E16.3.22.0")}),-1.0]])]});
            var Q46;
            Q46=makeQuery(id+"F5.imprint","IMPRINT",FACE,{"disambiguationData":[TD([[makeQuery(id+"F5.imprint","IMPRINT",EDGE,{"derivedFrom":sQuery(id+"F5.wireOp",EDGE,"E17.3.23.0")}),1.0]])]});
            var Q47;
            Q47=makeQuery(id+"F5.imprint","IMPRINT",FACE,{"disambiguationData":[TD([[makeQuery(id+"F5.imprint","IMPRINT",EDGE,{"derivedFrom":sQuery(id+"F5.wireOp",EDGE,"E17.3.23.0")}),-1.0]])]});
            var Q48;
            Q48=makeQuery(id+"F5.imprint","IMPRINT",FACE,{"disambiguationData":[TD([[makeQuery(id+"F5.imprint","IMPRINT",EDGE,{"derivedFrom":sQuery(id+"F5.wireOp",EDGE,"E17.3.24.0")}),1.0]])]});
            var Q49;
            Q49=makeQuery(id+"F5.imprint","IMPRINT",FACE,{"disambiguationData":[TD([[makeQuery(id+"F5.imprint","IMPRINT",EDGE,{"derivedFrom":sQuery(id+"F5.wireOp",EDGE,"E17.3.24.0")}),-1.0]])]});
            var Q50;
            Q50=makeQuery(id+"F5.imprint","IMPRINT",FACE,{"disambiguationData":[TD([[makeQuery(id+"F5.imprint","IMPRINT",EDGE,{"derivedFrom":sQuery(id+"F5.wireOp",EDGE,"E18.3.25.0")}),1.0]])]});
            var Q51;
            Q51=makeQuery(id+"F5.imprint","IMPRINT",FACE,{"disambiguationData":[TD([[makeQuery(id+"F5.imprint","IMPRINT",EDGE,{"derivedFrom":sQuery(id+"F5.wireOp",EDGE,"E18.3.25.0")}),-1.0]])]});
            var Q52;
            Q52=makeQuery(id+"F5.imprint","IMPRINT",FACE,{"disambiguationData":[TD([[makeQuery(id+"F5.imprint","IMPRINT",EDGE,{"derivedFrom":sQuery(id+"F5.wireOp",EDGE,"E18.3.26.0")}),1.0]])]});
            var Q53;
            Q53=makeQuery(id+"F5.imprint","IMPRINT",FACE,{"disambiguationData":[TD([[makeQuery(id+"F5.imprint","IMPRINT",EDGE,{"derivedFrom":sQuery(id+"F5.wireOp",EDGE,"E18.3.26.0")}),-1.0]])]});
            var Q54;
            Q54=makeQuery(id+"F5.imprint","IMPRINT",FACE,{"disambiguationData":[TD([[makeQuery(id+"F5.imprint","IMPRINT",EDGE,{"derivedFrom":sQuery(id+"F5.wireOp",EDGE,"E18.3.27.0")}),1.0]])]});
            var Q55;
            Q55=makeQuery(id+"F5.imprint","IMPRINT",FACE,{"disambiguationData":[TD([[makeQuery(id+"F5.imprint","IMPRINT",EDGE,{"derivedFrom":sQuery(id+"F5.wireOp",EDGE,"E18.3.27.0")}),-1.0]])]});
            var Q56;
            Q56=makeQuery(id+"F5.imprint","IMPRINT",FACE,{"disambiguationData":[TD([[makeQuery(id+"F5.imprint","IMPRINT",EDGE,{"derivedFrom":sQuery(id+"F5.wireOp",EDGE,"7cc6724f-c960-404d-9fb9-fa70a4dc17af.0")}),1.0]])]});
            var Q57;
            Q57=makeQuery(id+"F5.imprint","IMPRINT",FACE,{"disambiguationData":[TD([[makeQuery(id+"F5.imprint","IMPRINT",EDGE,{"derivedFrom":sQuery(id+"F5.wireOp",EDGE,"E19.3.28.0")}),1.0]])]});
            var Q58;
            Q58=makeQuery(id+"F5.imprint","IMPRINT",FACE,{"disambiguationData":[TD([[makeQuery(id+"F5.imprint","IMPRINT",EDGE,{"derivedFrom":sQuery(id+"F5.wireOp",EDGE,"E19.3.28.0")}),-1.0]])]});
            var Q59;
            Q59=makeQuery(id+"F5.imprint","IMPRINT",FACE,{"disambiguationData":[TD([[makeQuery(id+"F5.imprint","IMPRINT",EDGE,{"derivedFrom":sQuery(id+"F5.wireOp",EDGE,"E19.3.29.0")}),1.0]])]});
            var Q60;
            Q60=makeQuery(id+"F5.imprint","IMPRINT",FACE,{"disambiguationData":[TD([[makeQuery(id+"F5.imprint","IMPRINT",EDGE,{"derivedFrom":sQuery(id+"F5.wireOp",EDGE,"E19.3.29.0")}),-1.0]])]});
            var Q61;
            Q61=makeQuery(id+"F5.imprint","IMPRINT",FACE,{"disambiguationData":[TD([[makeQuery(id+"F5.imprint","IMPRINT",EDGE,{"derivedFrom":sQuery(id+"F5.wireOp",EDGE,"E22.0")}),1.0]])]});
            extrude(context, id + "F6", {"entities" : qUnion([Q0, Q1, Q2, Q3, Q4, Q5, Q6, Q7, Q8, Q9, Q10, Q11, Q12, Q13, Q14, Q15, Q16, Q17, Q18, Q19, Q20, Q21, Q22, Q23, Q24, Q25, Q26, Q27, Q28, Q29, Q30, Q31, Q32, Q33, Q34, Q35, Q36, Q37, Q38, Q39, Q40, Q41, Q42, Q43, Q44, Q45, Q46, Q47, Q48, Q49, Q50, Q51, Q52, Q53, Q54, Q55, Q56, Q57, Q58, Q59, Q60, Q61]), "operationType" : NewBodyOperationType.REMOVE, "oppositeDirection" : true, "depth" : 15 * mm});
        }
        {
            var Q0;
            Q0=makeQuery(id+"F5.imprint","IMPRINT",FACE,{"disambiguationData":[TD([[makeQuery(id+"F5.imprint","IMPRINT",EDGE,{"derivedFrom":sQuery(id+"F5.wireOp",EDGE,"E7")}),-1.0]])]});
            var Q1;
            Q1=makeQuery(id+"F5.imprint","IMPRINT",FACE,{"disambiguationData":[TD([[makeQuery(id+"F5.imprint","IMPRINT",EDGE,{"derivedFrom":sQuery(id+"F5.wireOp",EDGE,"E15.1.0.1")}),1.0]])]});
            var Q2;
            Q2=makeQuery(id+"F5.imprint","IMPRINT",FACE,{"disambiguationData":[TD([[makeQuery(id+"F5.imprint","IMPRINT",EDGE,{"derivedFrom":sQuery(id+"F5.wireOp",EDGE,"E15.2.0.1")}),1.0]])]});
            var Q3;
            Q3=makeQuery(id+"F5.imprint","IMPRINT",FACE,{"disambiguationData":[TD([[makeQuery(id+"F5.imprint","IMPRINT",EDGE,{"derivedFrom":sQuery(id+"F5.wireOp",EDGE,"E16.3.3.0")}),1.0]])]});
            var Q4;
            Q4=makeQuery(id+"F5.imprint","IMPRINT",FACE,{"disambiguationData":[TD([[makeQuery(id+"F5.imprint","IMPRINT",EDGE,{"derivedFrom":sQuery(id+"F5.wireOp",EDGE,"E16.3.4.0")}),1.0]])]});
            var Q5;
            Q5=makeQuery(id+"F5.imprint","IMPRINT",FACE,{"disambiguationData":[TD([[makeQuery(id+"F5.imprint","IMPRINT",EDGE,{"derivedFrom":sQuery(id+"F5.wireOp",EDGE,"E16.3.5.0")}),1.0]])]});
            var Q6;
            Q6=makeQuery(id+"F5.imprint","IMPRINT",FACE,{"disambiguationData":[TD([[makeQuery(id+"F5.imprint","IMPRINT",EDGE,{"derivedFrom":sQuery(id+"F5.wireOp",EDGE,"E16.3.6.0")}),1.0]])]});
            var Q7;
            Q7=makeQuery(id+"F5.imprint","IMPRINT",FACE,{"disambiguationData":[TD([[makeQuery(id+"F5.imprint","IMPRINT",EDGE,{"derivedFrom":sQuery(id+"F5.wireOp",EDGE,"E16.3.7.0")}),1.0]])]});
            var Q8;
            Q8=makeQuery(id+"F5.imprint","IMPRINT",FACE,{"disambiguationData":[TD([[makeQuery(id+"F5.imprint","IMPRINT",EDGE,{"derivedFrom":sQuery(id+"F5.wireOp",EDGE,"E16.3.8.0")}),1.0]])]});
            var Q9;
            Q9=makeQuery(id+"F5.imprint","IMPRINT",FACE,{"disambiguationData":[TD([[makeQuery(id+"F5.imprint","IMPRINT",EDGE,{"derivedFrom":sQuery(id+"F5.wireOp",EDGE,"E16.3.9.0")}),1.0]])]});
            var Q10;
            Q10=makeQuery(id+"F5.imprint","IMPRINT",FACE,{"disambiguationData":[TD([[makeQuery(id+"F5.imprint","IMPRINT",EDGE,{"derivedFrom":sQuery(id+"F5.wireOp",EDGE,"E16.3.10.0")}),1.0]])]});
            var Q11;
            Q11=makeQuery(id+"F5.imprint","IMPRINT",FACE,{"disambiguationData":[TD([[makeQuery(id+"F5.imprint","IMPRINT",EDGE,{"derivedFrom":sQuery(id+"F5.wireOp",EDGE,"E16.3.11.0")}),1.0]])]});
            var Q12;
            Q12=makeQuery(id+"F5.imprint","IMPRINT",FACE,{"disambiguationData":[TD([[makeQuery(id+"F5.imprint","IMPRINT",EDGE,{"derivedFrom":sQuery(id+"F5.wireOp",EDGE,"E16.3.12.0")}),1.0]])]});
            var Q13;
            Q13=makeQuery(id+"F5.imprint","IMPRINT",FACE,{"disambiguationData":[TD([[makeQuery(id+"F5.imprint","IMPRINT",EDGE,{"derivedFrom":sQuery(id+"F5.wireOp",EDGE,"E16.3.13.0")}),1.0]])]});
            var Q14;
            Q14=makeQuery(id+"F5.imprint","IMPRINT",FACE,{"disambiguationData":[TD([[makeQuery(id+"F5.imprint","IMPRINT",EDGE,{"derivedFrom":sQuery(id+"F5.wireOp",EDGE,"E16.3.14.0")}),1.0]])]});
            var Q15;
            Q15=makeQuery(id+"F5.imprint","IMPRINT",FACE,{"disambiguationData":[TD([[makeQuery(id+"F5.imprint","IMPRINT",EDGE,{"derivedFrom":sQuery(id+"F5.wireOp",EDGE,"E16.3.15.0")}),1.0]])]});
            var Q16;
            Q16=makeQuery(id+"F5.imprint","IMPRINT",FACE,{"disambiguationData":[TD([[makeQuery(id+"F5.imprint","IMPRINT",EDGE,{"derivedFrom":sQuery(id+"F5.wireOp",EDGE,"E16.3.16.0")}),1.0]])]});
            var Q17;
            Q17=makeQuery(id+"F5.imprint","IMPRINT",FACE,{"disambiguationData":[TD([[makeQuery(id+"F5.imprint","IMPRINT",EDGE,{"derivedFrom":sQuery(id+"F5.wireOp",EDGE,"E16.3.17.0")}),1.0]])]});
            var Q18;
            Q18=makeQuery(id+"F5.imprint","IMPRINT",FACE,{"disambiguationData":[TD([[makeQuery(id+"F5.imprint","IMPRINT",EDGE,{"derivedFrom":sQuery(id+"F5.wireOp",EDGE,"E16.3.18.0")}),1.0]])]});
            var Q19;
            Q19=makeQuery(id+"F5.imprint","IMPRINT",FACE,{"disambiguationData":[TD([[makeQuery(id+"F5.imprint","IMPRINT",EDGE,{"derivedFrom":sQuery(id+"F5.wireOp",EDGE,"E16.3.19.0")}),1.0]])]});
            var Q20;
            Q20=makeQuery(id+"F5.imprint","IMPRINT",FACE,{"disambiguationData":[TD([[makeQuery(id+"F5.imprint","IMPRINT",EDGE,{"derivedFrom":sQuery(id+"F5.wireOp",EDGE,"E16.3.20.0")}),1.0]])]});
            var Q21;
            Q21=makeQuery(id+"F5.imprint","IMPRINT",FACE,{"disambiguationData":[TD([[makeQuery(id+"F5.imprint","IMPRINT",EDGE,{"derivedFrom":sQuery(id+"F5.wireOp",EDGE,"E16.3.21.0")}),1.0]])]});
            var Q22;
            Q22=makeQuery(id+"F5.imprint","IMPRINT",FACE,{"disambiguationData":[TD([[makeQuery(id+"F5.imprint","IMPRINT",EDGE,{"derivedFrom":sQuery(id+"F5.wireOp",EDGE,"E16.3.22.0")}),1.0]])]});
            var Q23;
            Q23=makeQuery(id+"F5.imprint","IMPRINT",FACE,{"disambiguationData":[TD([[makeQuery(id+"F5.imprint","IMPRINT",EDGE,{"derivedFrom":sQuery(id+"F5.wireOp",EDGE,"E17.3.23.0")}),1.0]])]});
            var Q24;
            Q24=makeQuery(id+"F5.imprint","IMPRINT",FACE,{"disambiguationData":[TD([[makeQuery(id+"F5.imprint","IMPRINT",EDGE,{"derivedFrom":sQuery(id+"F5.wireOp",EDGE,"E17.3.24.0")}),1.0]])]});
            var Q25;
            Q25=makeQuery(id+"F5.imprint","IMPRINT",FACE,{"disambiguationData":[TD([[makeQuery(id+"F5.imprint","IMPRINT",EDGE,{"derivedFrom":sQuery(id+"F5.wireOp",EDGE,"E18.3.25.0")}),1.0]])]});
            var Q26;
            Q26=makeQuery(id+"F5.imprint","IMPRINT",FACE,{"disambiguationData":[TD([[makeQuery(id+"F5.imprint","IMPRINT",EDGE,{"derivedFrom":sQuery(id+"F5.wireOp",EDGE,"E18.3.26.0")}),1.0]])]});
            var Q27;
            Q27=makeQuery(id+"F5.imprint","IMPRINT",FACE,{"disambiguationData":[TD([[makeQuery(id+"F5.imprint","IMPRINT",EDGE,{"derivedFrom":sQuery(id+"F5.wireOp",EDGE,"E18.3.27.0")}),1.0]])]});
            var Q28;
            Q28=makeQuery(id+"F5.imprint","IMPRINT",FACE,{"disambiguationData":[TD([[makeQuery(id+"F5.imprint","IMPRINT",EDGE,{"derivedFrom":sQuery(id+"F5.wireOp",EDGE,"E19.3.28.0")}),1.0]])]});
            var Q29;
            Q29=makeQuery(id+"F5.imprint","IMPRINT",FACE,{"disambiguationData":[TD([[makeQuery(id+"F5.imprint","IMPRINT",EDGE,{"derivedFrom":sQuery(id+"F5.wireOp",EDGE,"E19.3.29.0")}),1.0]])]});
            var Q30;
            Q30=makeQuery(id+"F5.imprint","IMPRINT",FACE,{"disambiguationData":[TD([[makeQuery(id+"F5.imprint","IMPRINT",EDGE,{"derivedFrom":sQuery(id+"F5.wireOp",EDGE,"E22.0")}),1.0]])]});
            extrude(context, id + "F7", {"entities" : qUnion([Q0, Q1, Q2, Q3, Q4, Q5, Q6, Q7, Q8, Q9, Q10, Q11, Q12, Q13, Q14, Q15, Q16, Q17, Q18, Q19, Q20, Q21, Q22, Q23, Q24, Q25, Q26, Q27, Q28, Q29, Q30]), "depth" : 7 * mm, "hasSecondDirection" : true, "secondDirectionOppositeDirection" : true, "secondDirectionDepth" : 15 * mm});
        }
        {
            var Q0;
            Q0=makeQuery(id+"F5.imprint","IMPRINT",FACE,{"disambiguationData":[TD([[makeQuery(id+"F5.imprint","IMPRINT",EDGE,{"derivedFrom":sQuery(id+"F5.wireOp",EDGE,"E9.0")}),-1.0]])]});
            var Q1;
            Q1=makeQuery(id+"F5.imprint","IMPRINT",FACE,{"disambiguationData":[TD([[makeQuery(id+"F5.imprint","IMPRINT",EDGE,{"derivedFrom":sQuery(id+"F5.wireOp",EDGE,"E15.1.0.1")}),-1.0]])]});
            var Q2;
            Q2=makeQuery(id+"F5.imprint","IMPRINT",FACE,{"disambiguationData":[TD([[makeQuery(id+"F5.imprint","IMPRINT",EDGE,{"derivedFrom":sQuery(id+"F5.wireOp",EDGE,"E15.2.0.1")}),-1.0]])]});
            var Q3;
            Q3=makeQuery(id+"F5.imprint","IMPRINT",FACE,{"disambiguationData":[TD([[makeQuery(id+"F5.imprint","IMPRINT",EDGE,{"derivedFrom":sQuery(id+"F5.wireOp",EDGE,"E16.3.3.0")}),-1.0]])]});
            var Q4;
            Q4=makeQuery(id+"F5.imprint","IMPRINT",FACE,{"disambiguationData":[TD([[makeQuery(id+"F5.imprint","IMPRINT",EDGE,{"derivedFrom":sQuery(id+"F5.wireOp",EDGE,"E16.3.4.0")}),-1.0]])]});
            var Q5;
            Q5=makeQuery(id+"F5.imprint","IMPRINT",FACE,{"disambiguationData":[TD([[makeQuery(id+"F5.imprint","IMPRINT",EDGE,{"derivedFrom":sQuery(id+"F5.wireOp",EDGE,"E16.3.5.0")}),-1.0]])]});
            var Q6;
            Q6=makeQuery(id+"F5.imprint","IMPRINT",FACE,{"disambiguationData":[TD([[makeQuery(id+"F5.imprint","IMPRINT",EDGE,{"derivedFrom":sQuery(id+"F5.wireOp",EDGE,"E16.3.6.0")}),-1.0]])]});
            var Q7;
            Q7=makeQuery(id+"F5.imprint","IMPRINT",FACE,{"disambiguationData":[TD([[makeQuery(id+"F5.imprint","IMPRINT",EDGE,{"derivedFrom":sQuery(id+"F5.wireOp",EDGE,"E16.3.7.0")}),-1.0]])]});
            var Q8;
            Q8=makeQuery(id+"F5.imprint","IMPRINT",FACE,{"disambiguationData":[TD([[makeQuery(id+"F5.imprint","IMPRINT",EDGE,{"derivedFrom":sQuery(id+"F5.wireOp",EDGE,"E16.3.8.0")}),-1.0]])]});
            var Q9;
            Q9=makeQuery(id+"F5.imprint","IMPRINT",FACE,{"disambiguationData":[TD([[makeQuery(id+"F5.imprint","IMPRINT",EDGE,{"derivedFrom":sQuery(id+"F5.wireOp",EDGE,"E16.3.9.0")}),-1.0]])]});
            var Q10;
            Q10=makeQuery(id+"F5.imprint","IMPRINT",FACE,{"disambiguationData":[TD([[makeQuery(id+"F5.imprint","IMPRINT",EDGE,{"derivedFrom":sQuery(id+"F5.wireOp",EDGE,"E16.3.10.0")}),-1.0]])]});
            var Q11;
            Q11=makeQuery(id+"F5.imprint","IMPRINT",FACE,{"disambiguationData":[TD([[makeQuery(id+"F5.imprint","IMPRINT",EDGE,{"derivedFrom":sQuery(id+"F5.wireOp",EDGE,"E16.3.11.0")}),-1.0]])]});
            var Q12;
            Q12=makeQuery(id+"F5.imprint","IMPRINT",FACE,{"disambiguationData":[TD([[makeQuery(id+"F5.imprint","IMPRINT",EDGE,{"derivedFrom":sQuery(id+"F5.wireOp",EDGE,"E16.3.12.0")}),-1.0]])]});
            var Q13;
            Q13=makeQuery(id+"F5.imprint","IMPRINT",FACE,{"disambiguationData":[TD([[makeQuery(id+"F5.imprint","IMPRINT",EDGE,{"derivedFrom":sQuery(id+"F5.wireOp",EDGE,"E16.3.13.0")}),-1.0]])]});
            var Q14;
            Q14=makeQuery(id+"F5.imprint","IMPRINT",FACE,{"disambiguationData":[TD([[makeQuery(id+"F5.imprint","IMPRINT",EDGE,{"derivedFrom":sQuery(id+"F5.wireOp",EDGE,"E16.3.14.0")}),-1.0]])]});
            var Q15;
            Q15=makeQuery(id+"F5.imprint","IMPRINT",FACE,{"disambiguationData":[TD([[makeQuery(id+"F5.imprint","IMPRINT",EDGE,{"derivedFrom":sQuery(id+"F5.wireOp",EDGE,"E16.3.15.0")}),-1.0]])]});
            var Q16;
            Q16=makeQuery(id+"F5.imprint","IMPRINT",FACE,{"disambiguationData":[TD([[makeQuery(id+"F5.imprint","IMPRINT",EDGE,{"derivedFrom":sQuery(id+"F5.wireOp",EDGE,"E16.3.16.0")}),-1.0]])]});
            var Q17;
            Q17=makeQuery(id+"F5.imprint","IMPRINT",FACE,{"disambiguationData":[TD([[makeQuery(id+"F5.imprint","IMPRINT",EDGE,{"derivedFrom":sQuery(id+"F5.wireOp",EDGE,"E16.3.17.0")}),-1.0]])]});
            var Q18;
            Q18=makeQuery(id+"F5.imprint","IMPRINT",FACE,{"disambiguationData":[TD([[makeQuery(id+"F5.imprint","IMPRINT",EDGE,{"derivedFrom":sQuery(id+"F5.wireOp",EDGE,"E16.3.18.0")}),-1.0]])]});
            var Q19;
            Q19=makeQuery(id+"F5.imprint","IMPRINT",FACE,{"disambiguationData":[TD([[makeQuery(id+"F5.imprint","IMPRINT",EDGE,{"derivedFrom":sQuery(id+"F5.wireOp",EDGE,"E16.3.19.0")}),-1.0]])]});
            var Q20;
            Q20=makeQuery(id+"F5.imprint","IMPRINT",FACE,{"disambiguationData":[TD([[makeQuery(id+"F5.imprint","IMPRINT",EDGE,{"derivedFrom":sQuery(id+"F5.wireOp",EDGE,"E16.3.20.0")}),-1.0]])]});
            var Q21;
            Q21=makeQuery(id+"F5.imprint","IMPRINT",FACE,{"disambiguationData":[TD([[makeQuery(id+"F5.imprint","IMPRINT",EDGE,{"derivedFrom":sQuery(id+"F5.wireOp",EDGE,"E16.3.21.0")}),-1.0]])]});
            var Q22;
            Q22=makeQuery(id+"F5.imprint","IMPRINT",FACE,{"disambiguationData":[TD([[makeQuery(id+"F5.imprint","IMPRINT",EDGE,{"derivedFrom":sQuery(id+"F5.wireOp",EDGE,"E16.3.22.0")}),-1.0]])]});
            var Q23;
            Q23=makeQuery(id+"F5.imprint","IMPRINT",FACE,{"disambiguationData":[TD([[makeQuery(id+"F5.imprint","IMPRINT",EDGE,{"derivedFrom":sQuery(id+"F5.wireOp",EDGE,"E17.3.23.0")}),-1.0]])]});
            var Q24;
            Q24=makeQuery(id+"F5.imprint","IMPRINT",FACE,{"disambiguationData":[TD([[makeQuery(id+"F5.imprint","IMPRINT",EDGE,{"derivedFrom":sQuery(id+"F5.wireOp",EDGE,"E17.3.24.0")}),-1.0]])]});
            var Q25;
            Q25=makeQuery(id+"F5.imprint","IMPRINT",FACE,{"disambiguationData":[TD([[makeQuery(id+"F5.imprint","IMPRINT",EDGE,{"derivedFrom":sQuery(id+"F5.wireOp",EDGE,"E18.3.25.0")}),-1.0]])]});
            var Q26;
            Q26=makeQuery(id+"F5.imprint","IMPRINT",FACE,{"disambiguationData":[TD([[makeQuery(id+"F5.imprint","IMPRINT",EDGE,{"derivedFrom":sQuery(id+"F5.wireOp",EDGE,"E18.3.26.0")}),-1.0]])]});
            var Q27;
            Q27=makeQuery(id+"F5.imprint","IMPRINT",FACE,{"disambiguationData":[TD([[makeQuery(id+"F5.imprint","IMPRINT",EDGE,{"derivedFrom":sQuery(id+"F5.wireOp",EDGE,"E18.3.27.0")}),-1.0]])]});
            var Q28;
            Q28=makeQuery(id+"F5.imprint","IMPRINT",FACE,{"disambiguationData":[TD([[makeQuery(id+"F5.imprint","IMPRINT",EDGE,{"derivedFrom":sQuery(id+"F5.wireOp",EDGE,"E19.3.28.0")}),-1.0]])]});
            var Q29;
            Q29=makeQuery(id+"F5.imprint","IMPRINT",FACE,{"disambiguationData":[TD([[makeQuery(id+"F5.imprint","IMPRINT",EDGE,{"derivedFrom":sQuery(id+"F5.wireOp",EDGE,"E19.3.29.0")}),-1.0]])]});
            extrude(context, id + "F8", {"entities" : qUnion([Q0, Q1, Q2, Q3, Q4, Q5, Q6, Q7, Q8, Q9, Q10, Q11, Q12, Q13, Q14, Q15, Q16, Q17, Q18, Q19, Q20, Q21, Q22, Q23, Q24, Q25, Q26, Q27, Q28, Q29]), "depth" : 5 * mm, "hasSecondDirection" : true, "secondDirectionOppositeDirection" : true, "secondDirectionDepth" : 15 * mm});
        }
    });
